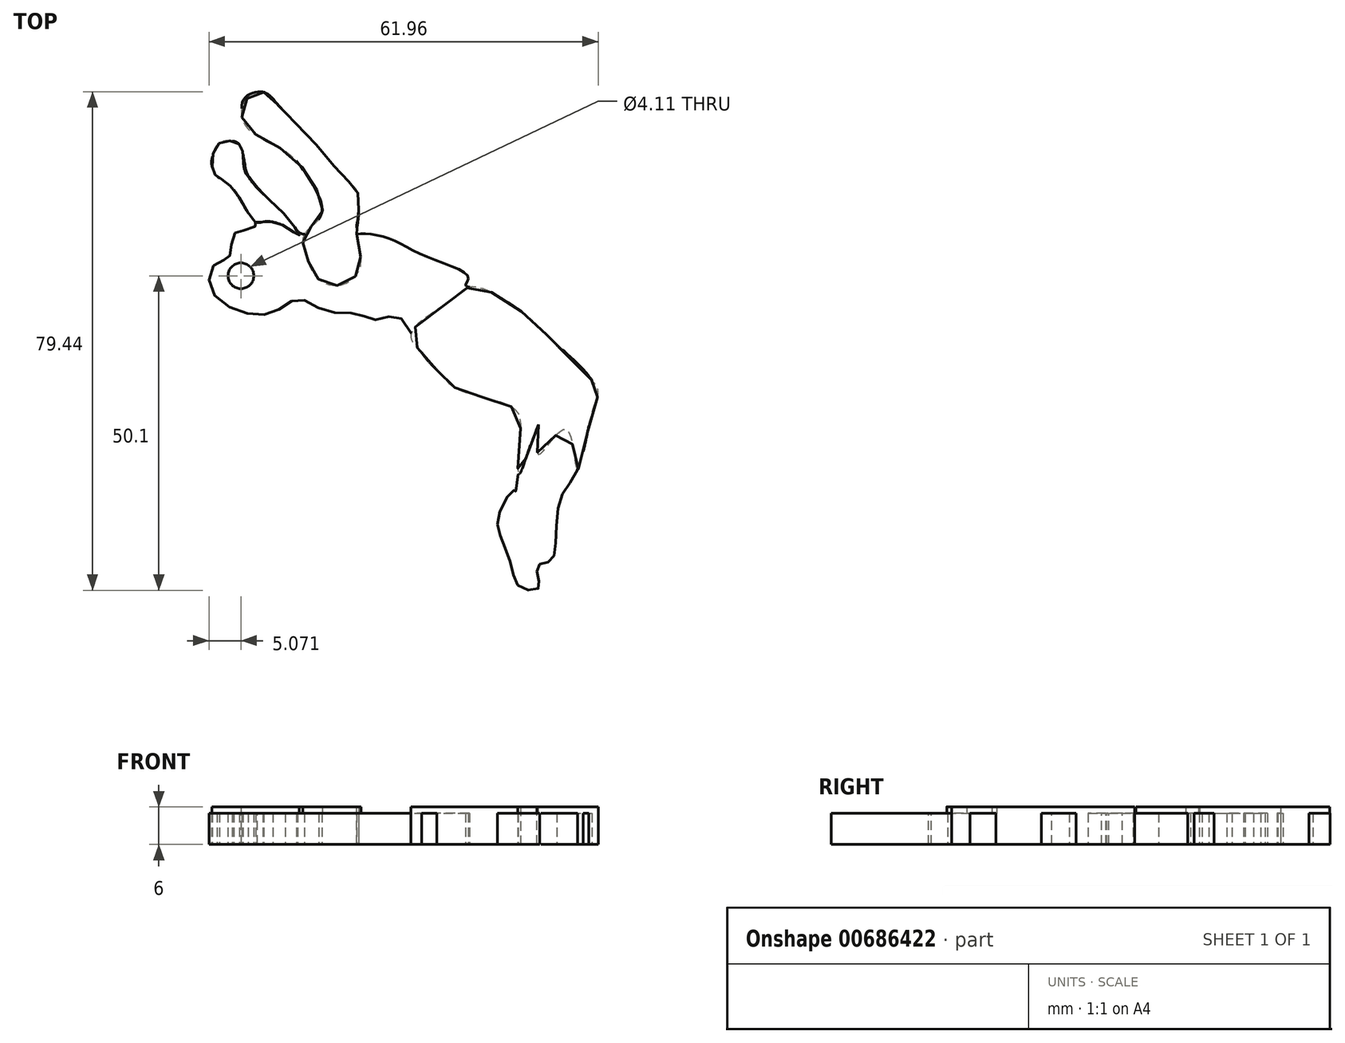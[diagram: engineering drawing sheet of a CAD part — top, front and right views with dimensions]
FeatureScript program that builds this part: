
annotation { "Feature Type Name" : "Feature", "Feature Type Description" : "" }
export const myFeature = defineFeature(function(context is Context, id is Id, definition is map)
    precondition{}
    {
        {
            var Q0;
            Q0=qCreatedBy(makeId("Top.planeOp"),FACE);
            var sketch = newSketch(context, id + "F0", { "sketchPlane" : qUnion([Q0])});
            skFitSpline(sketch, "E0", {"points": [v(-44.34, 44.57) * mm, v(-42.86, 44) * mm, v(-40.81, 41.78) * mm, v(-38.84, 39.64) * mm, v(-36.62, 37.18) * mm, v(-33.66, 34.06) * mm, v(-30.87, 30.52) * mm, v(-28.9, 28.14) * mm, v(-29.06, 22.47) * mm, v(-29.4, 21.82) * mm, v(-28.65, 21.9) * mm, v(-24.22, 21.32) * mm, v(-17.64, 18.2) * mm, v(-11.16, 15) * mm, v(-11.57, 13.68) * mm, v(-9.6, 13.27) * mm, v(-5.32, 10.8) * mm, v(1.58, 5.3) * mm, v(8.97, -2.25) * mm, v(8.56, -6.36) * mm, v(6.1, -15.97) * mm, v(3.47, -20.4) * mm, v(2.75, -27.74) * mm, v(1.77, -30.28) * mm, v(0, -30.87) * mm, v(0, -33.02) * mm, v(0, -34.58) * mm, v(-2.92, -34.39) * mm, v(-4.29, -31.07) * mm, v(-6.05, -26.18) * mm, v(-6.24, -22.66) * mm, v(-3.9, -18.95) * mm, v(-3.7, -19.34) * mm, v(-2.72, -7.42) * mm, v(-4.1, -5.28) * mm, v(-12.1, -2.34) * mm, v(-18.75, 3.32) * mm, v(-22.46, 8.8) * mm, v(-25.97, 8.2) * mm, v(-28.7, 9.18) * mm, v(-33.79, 9.57) * mm, v(-38.09, 11.53) * mm, v(-41.8, 9.57) * mm, v(-46.88, 9.38) * mm, v(-52.16, 13.1) * mm, v(-51.37, 17.2) * mm, v(-49.42, 17.98) * mm, v(-49.03, 19.15) * mm, v(-48.25, 22.08) * mm, v(-46.69, 22.47) * mm, v(-44.73, 23.45) * mm, v(-45.32, 24.03) * mm, v(-49.42, 30.09) * mm, v(-51.18, 31.07) * mm, v(-51.77, 34.58) * mm, v(-48.05, 36.54) * mm, v(-46.69, 32.63) * mm, v(-45.51, 30.28) * mm, v(-39.07, 23.06) * mm, v(-37.11, 21.88) * mm, v(-35.35, 23.64) * mm, v(-34.57, 26.77) * mm, v(-40.24, 35.36) * mm, v(-42, 36.15) * mm, v(-46.3, 39.27) * mm, v(-46.88, 43.38) * mm, v(-44.34, 44.57) * mm]});
            skCircle(sketch, "E1", {"center": v(-47.36, 15.23) * mm, "radius": 2.05 * mm});
            skFitSpline(sketch, "E2", {"points": [v(-11.86, 5.6) * mm, v(-7.38, 2.8) * mm, v(-8.69, 1.68) * mm, v(-10.18, 0) * mm, v(-14.3, 2.24) * mm, v(-13.55, 2.99) * mm, v(-11.86, 5.6) * mm]});
            skSolve(sketch);
        }
        {
            var Q0;
            Q0=qCreatedBy(makeId("Top.planeOp"),FACE);
            var sketch = newSketch(context, id + "F1", { "sketchPlane" : qUnion([Q0])});
            skFitSpline(sketch, "E3", {"points": [v(-28.9, 21.9) * mm, v(-28.52, 27.17) * mm, v(-29.1, 29.1) * mm, v(-31.25, 31.26) * mm, v(-35.74, 36.54) * mm, v(-41.41, 42.4) * mm, v(-43.96, 44.51) * mm, v(-46.89, 42.85) * mm, v(-46.45, 38.94) * mm, v(-40.3, 35.07) * mm, v(-35.33, 28.94) * mm, v(-34.57, 24.8) * mm, v(-37.32, 21.7) * mm, v(-36.92, 18.36) * mm, v(-34.97, 14.65) * mm, v(-31.05, 13.86) * mm, v(-28.3, 16.8) * mm, v(-28.9, 21.9) * mm]});
            skSolve(sketch);
        }
        {
            var Q0;
            Q0=qCreatedBy(makeId("Top.planeOp"),FACE);
            var sketch = newSketch(context, id + "F2", { "sketchPlane" : qUnion([Q0])});
            skFitSpline(sketch, "E4", {"points": [v(-45.12, 23.84) * mm, v(-43.75, 23.84) * mm, v(-40.63, 23.25) * mm, v(-38.09, 21.69) * mm, v(-40.63, 25.2) * mm, v(-46.61, 31.65) * mm, v(-47.08, 35.14) * mm, v(-48.25, 36.54) * mm, v(-51.14, 36.07) * mm, v(-51.83, 32.04) * mm, v(-50.97, 30.93) * mm, v(-48.38, 28.83) * mm, v(-45.12, 23.84) * mm]});
            skSolve(sketch);
        }
        {
            var Q0;
            Q0=qCreatedBy(makeId("Top.planeOp"),FACE);
            var sketch = newSketch(context, id + "F3", { "sketchPlane" : qUnion([Q0])});
            skFitSpline(sketch, "E5", {"points": [v(0, -8.49) * mm, v(0, -13.21) * mm, v(4.29, -9.19) * mm, v(6.15, -15.63) * mm, v(8.5, -6.84) * mm, v(9.48, -2.93) * mm, v(7.13, 0) * mm, v(1.66, 5.47) * mm, v(-4.6, 10.94) * mm, v(-10.65, 13.48) * mm, v(-13.38, 11.72) * mm, v(-20.22, 6.06) * mm, v(-18.27, 2.74) * mm, v(-14.56, -1.56) * mm, v(-11.04, -3.52) * mm, v(-4.2, -5.67) * mm, v(-2.83, -9.57) * mm, v(-3.03, -16.41) * mm, v(0, -8.49) * mm]});
            skSolve(sketch);
        }
        {
            var Q0;
            Q0 = qSketchRegion(id + "F0", true);
            extrude(context, id + "F4", {"entities" : qUnion([Q0]), "depth" : 5 * mm, "offsetDistance" : 25.4 * mm});
        }
        {
            var Q0;
            Q0 = qSketchRegion(id + "F1", true);
            extrude(context, id + "F5", {"entities" : qUnion([Q0]), "operationType" : NewBodyOperationType.ADD, "depth" : 6 * mm, "offsetDistance" : 25.4 * mm});
        }
        {
            var Q0;
            Q0 = qSketchRegion(id + "F2", true);
            extrude(context, id + "F6", {"entities" : qUnion([Q0]), "operationType" : NewBodyOperationType.ADD, "depth" : 6 * mm, "offsetDistance" : 25.4 * mm});
        }
        {
            var Q0;
            Q0 = qSketchRegion(id + "F3", true);
            extrude(context, id + "F7", {"entities" : qUnion([Q0]), "operationType" : NewBodyOperationType.ADD, "depth" : 6 * mm, "offsetDistance" : 25.4 * mm});
        }
    });
